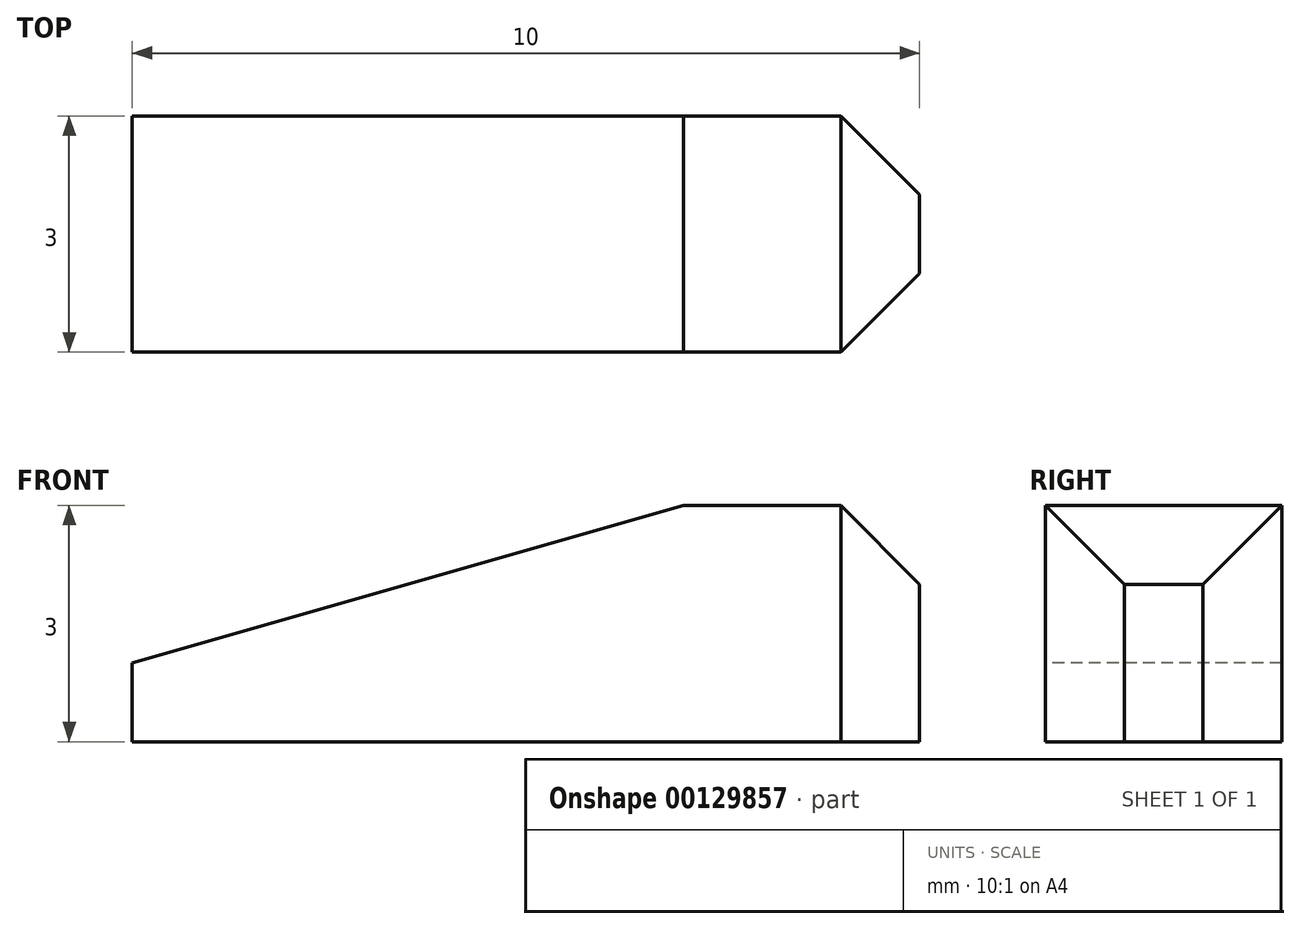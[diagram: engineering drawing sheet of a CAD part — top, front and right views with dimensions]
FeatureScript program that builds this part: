
annotation { "Feature Type Name" : "Feature", "Feature Type Description" : "" }
export const myFeature = defineFeature(function(context is Context, id is Id, definition is map)
    precondition{}
    {
        {
            var Q0;
            Q0=qCreatedBy(makeId("Top.planeOp"),FACE);
            var sketch = newSketch(context, id + "F0", { "sketchPlane" : qUnion([Q0])});
            skLineSegment(sketch, "E0.bottom", {"start": v(5, -1.5) * mm, "end": v(-5, -1.5) * mm});
            skLineSegment(sketch, "E0.top", {"start": v(5, 1.5) * mm, "end": v(-5, 1.5) * mm});
            skLineSegment(sketch, "E0.left", {"start": v(5, -1.5) * mm, "end": v(5, 1.5) * mm});
            skLineSegment(sketch, "E0.right", {"start": v(-5, -1.5) * mm, "end": v(-5, 1.5) * mm});
            skPoint(sketch, "E0.middle", {"position": v(0, 0) * mm});
            skSolve(sketch);
        }
        {
            var Q0;
            Q0=qSketchRegion(id+"F0",true);
            var Q1;
            Q1=makeQuery(id+"F0.imprint","IMPRINT",FACE,{"disambiguationData":[TD([[makeQuery(id+"F0.imprint","IMPRINT",EDGE,{"derivedFrom":sQuery(id+"F0.wireOp",EDGE,"E0.bottom")}),-1.0]])]});
            extrude(context, id + "F1", {"entities" : qUnion([Q0, Q1]), "depth" : 3 * mm});
        }
        {
            var Q0;
            Q0=makeQuery(id+"F1.opExtrude","SWEPT_FACE",FACE,{"disambiguationData":[OSD([sQuery(id+"F0.wireOp",EDGE,"E0.bottom")])]});
            var sketch = newSketch(context, id + "F2", { "sketchPlane" : qUnion([Q0])});
            skPoint(sketch, "E1", {"position": v(-5, 1) * mm});
            skPoint(sketch, "E2", {"position": v(2, 3) * mm});
            skLineSegment(sketch, "E3", {"start": v(-5, 1) * mm, "end": v(2, 3) * mm});
            skLineSegment(sketch, "E4", {"start": v(-5, 1) * mm, "end": v(-5, 3) * mm});
            skLineSegment(sketch, "E5", {"start": v(-5, 3) * mm, "end": v(2, 3) * mm});
            skSolve(sketch);
        }
        {
            var Q0;
            Q0 = qSketchRegion(id + "F2", true);
            extrude(context, id + "F3", {"entities" : qUnion([Q0]), "operationType" : NewBodyOperationType.REMOVE, "oppositeDirection" : true, "depth" : 25 * mm});
        }
        {
            var Q0;
            Q0=makeQuery(id+"F1.opExtrude","CAP_EDGE",EDGE,{"disambiguationData":[OSD([sQuery(id+"F0.wireOp",EDGE,"E0.left")])],"isStart":false});
            var Q1;
            Q1=makeQuery(id+"F1.opExtrude","SWEPT_EDGE",EDGE,{"disambiguationData":[OSD([sQuery(id+"F0.wireOp",EDGE,"E0.bottom"),sQuery(id+"F0.wireOp",EDGE,"E0.left")])]});
            var Q2;
            Q2=makeQuery(id+"F1.opExtrude","SWEPT_EDGE",EDGE,{"disambiguationData":[OSD([sQuery(id+"F0.wireOp",EDGE,"E0.top"),sQuery(id+"F0.wireOp",EDGE,"E0.left")])]});
            chamfer(context, id + "F4", {"entities" : qUnion([Q0, Q1, Q2]), "width" : 1 * mm, "tangentPropagation" : true});
        }
    });
